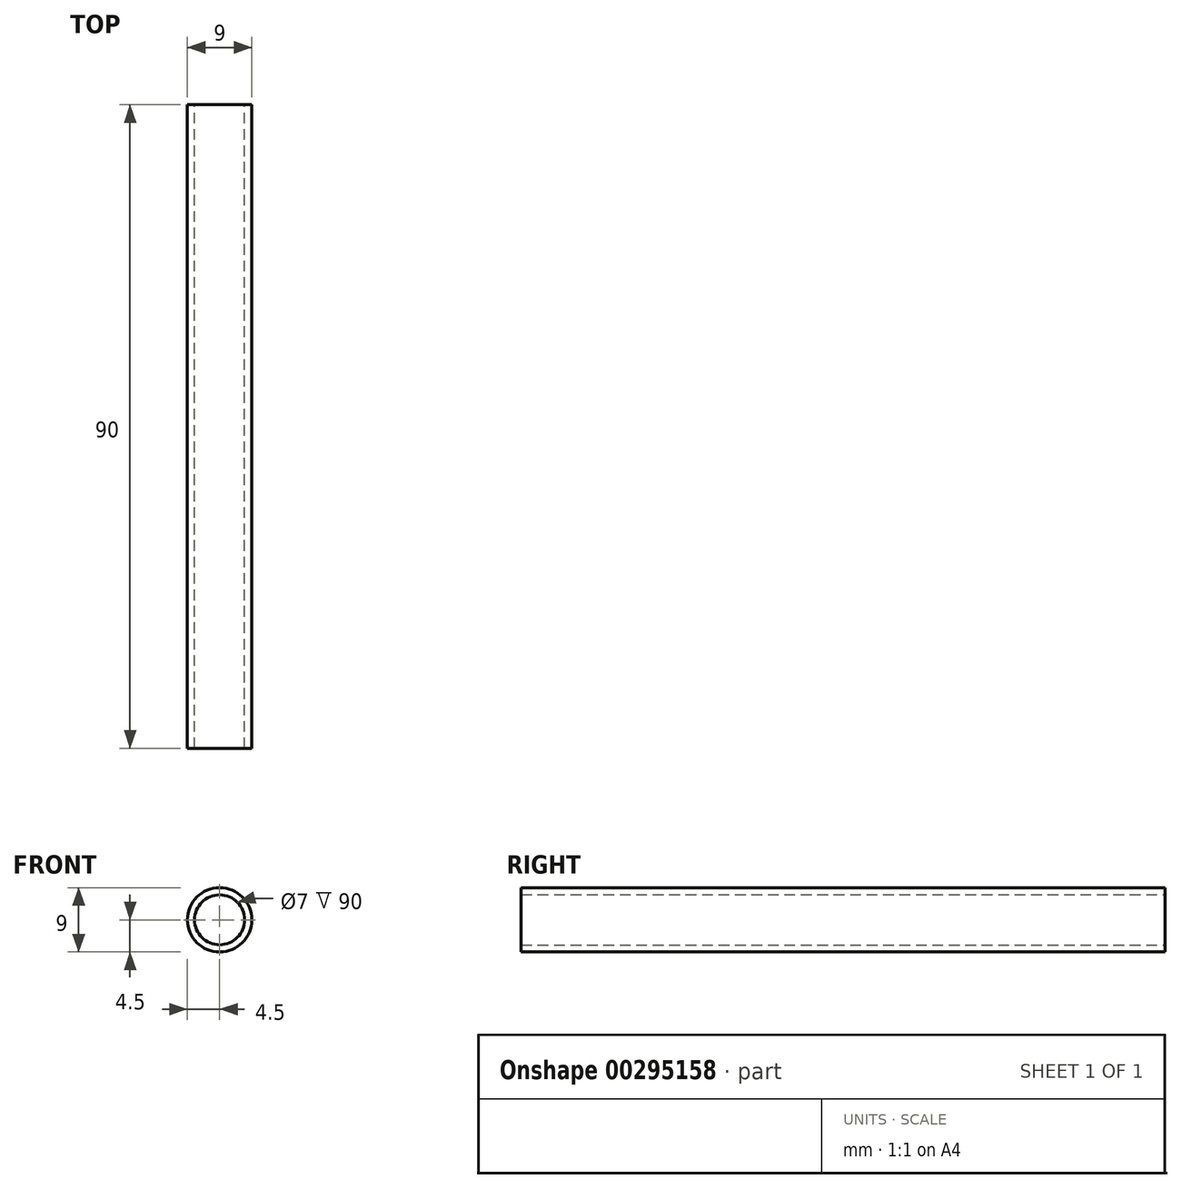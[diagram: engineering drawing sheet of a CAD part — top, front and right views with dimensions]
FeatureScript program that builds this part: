
annotation { "Feature Type Name" : "Feature", "Feature Type Description" : "" }
export const myFeature = defineFeature(function(context is Context, id is Id, definition is map)
    precondition{}
    {
        {
            var Q0;
            Q0=qCreatedBy(makeId("Front.planeOp"),FACE);
            var sketch = newSketch(context, id + "F0", { "sketchPlane" : qUnion([Q0])});
            skCircle(sketch, "E0", {"center": v(0, 0) * mm, "radius": 4.5 * mm});
            skSolve(sketch);
        }
        {
            var Q0;
            Q0=makeQuery(id+"F0.imprint","IMPRINT",FACE,{"disambiguationData":[TD([[makeQuery(id+"F0.imprint","IMPRINT",EDGE,{"derivedFrom":sQuery(id+"F0.wireOp",EDGE,"E0")}),1.0]])]});
            extrude(context, id + "F1", {"entities" : qUnion([Q0]), "endBound" : BoundingType.SYMMETRIC, "depth" : 90 * mm});
        }
        {
            var Q0;
            Q0=makeQuery(id+"F1.opExtrude","CAP_FACE",FACE,{"disambiguationData":[OSD([sQuery(id+"F0.wireOp",EDGE,"E0")])],"isStart":false});
            var Q1;
            Q1=makeQuery(id+"F1.opExtrude","CAP_FACE",FACE,{"disambiguationData":[OSD([sQuery(id+"F0.wireOp",EDGE,"E0")])],"isStart":true});
            var Q2;
            Q2=makeQuery(id+"F1.opExtrude","SWEPT_BODY",BODY,{"disambiguationData":[OSD([sQuery(id+"F0.wireOp",EDGE,"E0")])]});
            shell(context, id + "F2", {"entities" : qUnion([Q0, Q1]), "parts" : qUnion([Q2]), "thickness" : 1 * mm});
        }
    });
